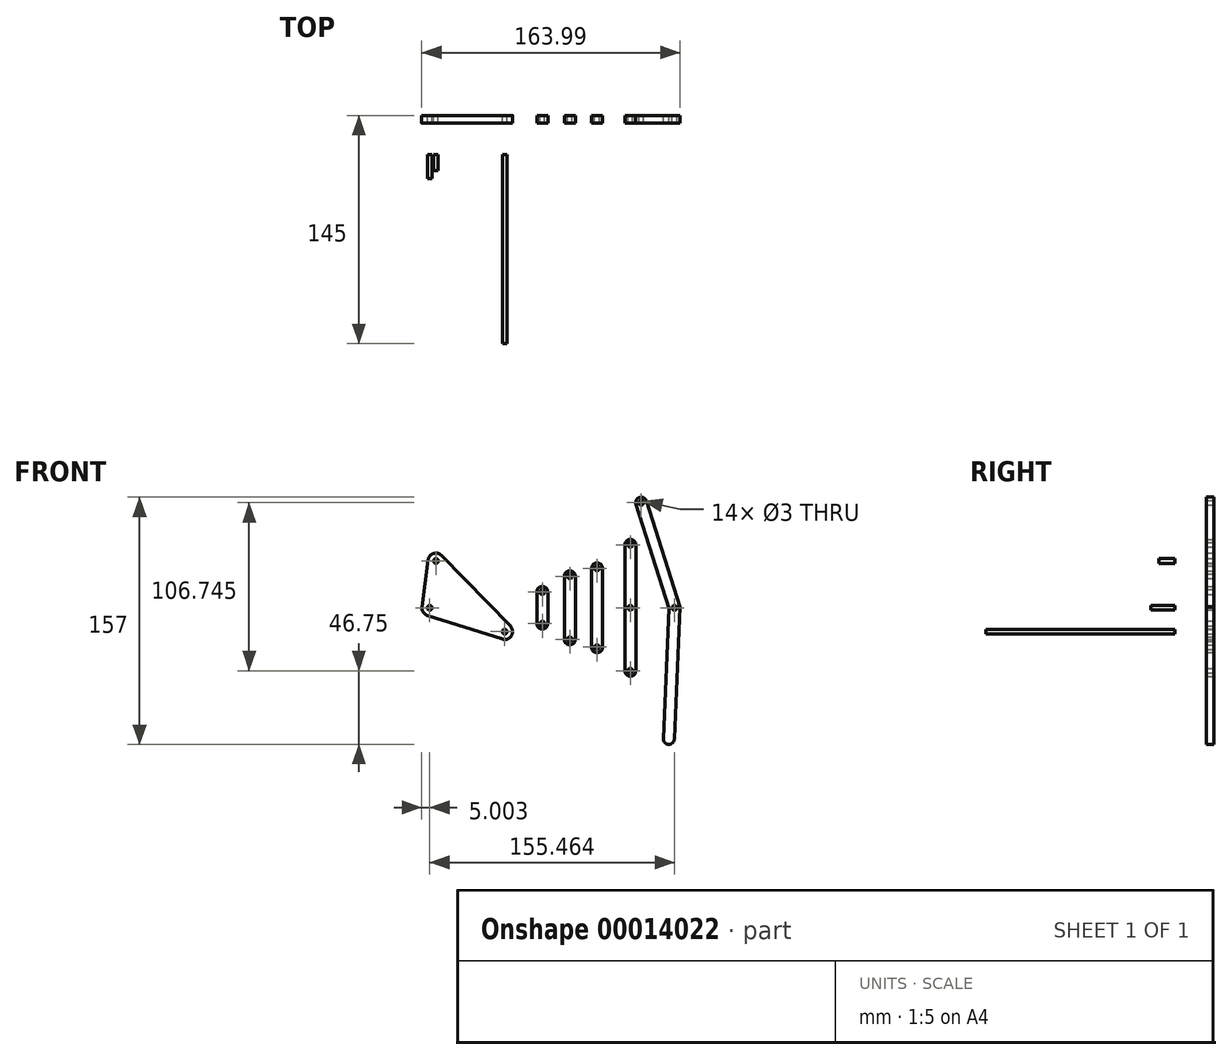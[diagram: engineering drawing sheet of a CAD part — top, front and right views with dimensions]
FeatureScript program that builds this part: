
annotation { "Feature Type Name" : "Feature", "Feature Type Description" : "" }
export const myFeature = defineFeature(function(context is Context, id is Id, definition is map)
    precondition{}
    {
        {
            var Q0;
            Q0=qCreatedBy(makeId("Front.planeOp"),FACE);
            var sketch = newSketch(context, id + "F0", { "sketchPlane" : qUnion([Q0])});
            skLineSegment(sketch, "E0", {"start": v(-62.83, 10) * mm, "end": v(-62.83, -10) * mm, "construction": true});
            skLineSegment(sketch, "E1", {"start": v(-45.34, 20) * mm, "end": v(-45.34, -20) * mm, "construction": true});
            skLineSegment(sketch, "E2", {"start": v(-28.03, 25) * mm, "end": v(-28.03, -25) * mm, "construction": true});
            skLineSegment(sketch, "E3", {"start": v(-6.9, 40) * mm, "end": v(-6.9, -40) * mm, "construction": true});
            skLineSegment(sketch, "E4", {"start": v(0, 66.75) * mm, "end": v(21.1, 0) * mm, "construction": true});
            skLineSegment(sketch, "E5", {"start": v(21.1, 0) * mm, "end": v(17.52, -83.25) * mm, "construction": true});
            skPoint(sketch, "E6", {"position": v(-62.83, 0) * mm});
            skPoint(sketch, "E7", {"position": v(-45.34, 0) * mm});
            skPoint(sketch, "E8", {"position": v(-28.03, 0) * mm});
            skPoint(sketch, "E9", {"position": v(-6.9, 0) * mm});
            skLineSegment(sketch, "E10", {"start": v(-130.38, 29.73) * mm, "end": v(-134.37, 0) * mm, "construction": true});
            skLineSegment(sketch, "E11", {"start": v(-134.37, 0) * mm, "end": v(-86.72, -15.14) * mm, "construction": true});
            skLineSegment(sketch, "E12", {"start": v(-86.72, -15.14) * mm, "end": v(-130.38, 29.73) * mm, "construction": true});
            skCircle(sketch, "E13", {"center": v(-62.83, 10) * mm, "radius": 1.5 * mm});
            skCircle(sketch, "E14", {"center": v(-62.83, -10) * mm, "radius": 1.5 * mm});
            skCircle(sketch, "E15", {"center": v(-45.34, -20) * mm, "radius": 1.5 * mm});
            skCircle(sketch, "E16", {"center": v(-45.34, 20) * mm, "radius": 1.5 * mm});
            skCircle(sketch, "E17", {"center": v(-28.03, 25) * mm, "radius": 1.5 * mm});
            skCircle(sketch, "E18", {"center": v(-28.03, -25) * mm, "radius": 1.5 * mm});
            skCircle(sketch, "E19", {"center": v(-6.9, 40) * mm, "radius": 1.5 * mm});
            skCircle(sketch, "E20", {"center": v(-6.9, -40) * mm, "radius": 1.5 * mm});
            skCircle(sketch, "E21", {"center": v(-6.9, 0) * mm, "radius": 1.5 * mm});
            skCircle(sketch, "E22", {"center": v(21.1, 0) * mm, "radius": 1.5 * mm});
            skCircle(sketch, "E23", {"center": v(0, 66.75) * mm, "radius": 1.5 * mm});
            skCircle(sketch, "E24", {"center": v(-130.38, 29.73) * mm, "radius": 1.5 * mm});
            skCircle(sketch, "E25", {"center": v(-134.37, 0) * mm, "radius": 1.5 * mm});
            skCircle(sketch, "E26", {"center": v(-86.72, -15.14) * mm, "radius": 1.5 * mm});
            skLineSegment(sketch, "E27.bottom", {"start": v(-66.33, 10) * mm, "end": v(-59.33, 10) * mm, "construction": true});
            skLineSegment(sketch, "E27.top", {"start": v(-66.33, -10) * mm, "end": v(-59.33, -10) * mm, "construction": true});
            skLineSegment(sketch, "E27.left", {"start": v(-66.33, 10) * mm, "end": v(-66.33, -10) * mm});
            skLineSegment(sketch, "E27.right", {"start": v(-59.33, 10) * mm, "end": v(-59.33, -10) * mm});
            skLineSegment(sketch, "E28.bottom", {"start": v(-48.84, 20) * mm, "end": v(-41.84, 20) * mm, "construction": true});
            skLineSegment(sketch, "E28.top", {"start": v(-48.84, -20) * mm, "end": v(-41.84, -20) * mm, "construction": true});
            skLineSegment(sketch, "E28.left", {"start": v(-48.84, 20) * mm, "end": v(-48.84, -20) * mm});
            skLineSegment(sketch, "E28.right", {"start": v(-41.84, 20) * mm, "end": v(-41.84, -20) * mm});
            skLineSegment(sketch, "E29.bottom", {"start": v(-31.53, 25) * mm, "end": v(-24.53, 25) * mm, "construction": true});
            skLineSegment(sketch, "E29.top", {"start": v(-31.53, -25) * mm, "end": v(-24.53, -25) * mm, "construction": true});
            skLineSegment(sketch, "E29.left", {"start": v(-31.53, 25) * mm, "end": v(-31.53, -25) * mm});
            skLineSegment(sketch, "E29.right", {"start": v(-24.53, 25) * mm, "end": v(-24.53, -25) * mm});
            skLineSegment(sketch, "E30.bottom", {"start": v(-10.4, 40) * mm, "end": v(-3.4, 40) * mm, "construction": true});
            skLineSegment(sketch, "E30.top", {"start": v(-10.4, -40) * mm, "end": v(-3.4, -40) * mm, "construction": true});
            skLineSegment(sketch, "E30.left", {"start": v(-10.4, 40) * mm, "end": v(-10.4, -40) * mm});
            skLineSegment(sketch, "E30.right", {"start": v(-3.4, 40) * mm, "end": v(-3.4, -40) * mm});
            skArc(sketch, "E31", {"start": v(-3.4, 40) * mm, "mid": v(-6.9, 43.5) * mm, "end": v(-10.4, 40) * mm});
            skArc(sketch, "E32", {"start": v(-24.53, 25) * mm, "mid": v(-28.03, 28.5) * mm, "end": v(-31.53, 25) * mm});
            skArc(sketch, "E33", {"start": v(-41.84, 20) * mm, "mid": v(-45.34, 23.5) * mm, "end": v(-48.84, 20) * mm});
            skArc(sketch, "E34", {"start": v(-59.33, 10) * mm, "mid": v(-62.83, 13.5) * mm, "end": v(-66.33, 10) * mm});
            skArc(sketch, "E35", {"start": v(-66.33, -10) * mm, "mid": v(-62.83, -13.5) * mm, "end": v(-59.33, -10) * mm});
            skArc(sketch, "E36", {"start": v(-48.84, -20) * mm, "mid": v(-45.34, -23.5) * mm, "end": v(-41.84, -20) * mm});
            skArc(sketch, "E37", {"start": v(-31.53, -25) * mm, "mid": v(-28.03, -28.5) * mm, "end": v(-24.53, -25) * mm});
            skArc(sketch, "E38", {"start": v(-10.4, -40) * mm, "mid": v(-6.9, -43.5) * mm, "end": v(-3.4, -40) * mm});
            skLineSegment(sketch, "E39.bottom", {"start": v(-3.34, 65.7) * mm, "end": v(3.34, 67.8) * mm, "construction": true});
            skLineSegment(sketch, "E39.top", {"start": v(17.57, -0.47) * mm, "end": v(24.62, 0.47) * mm, "construction": true});
            skLineSegment(sketch, "E39.left", {"start": v(3.34, 67.8) * mm, "end": v(24.62, 0.47) * mm});
            skLineSegment(sketch, "E39.right", {"start": v(-3.34, 65.7) * mm, "end": v(17.57, -0.47) * mm});
            skArc(sketch, "E40", {"start": v(3.34, 67.8) * mm, "mid": v(-1.05, 70.08) * mm, "end": v(-3.34, 65.7) * mm});
            skLineSegment(sketch, "E41", {"start": v(14.02, -83.1) * mm, "end": v(21.02, -83.4) * mm, "construction": true});
            skLineSegment(sketch, "E42", {"start": v(14.02, -83.1) * mm, "end": v(17.57, -0.47) * mm});
            skLineSegment(sketch, "E43", {"start": v(24.62, 0.47) * mm, "end": v(21.02, -83.4) * mm});
            skArc(sketch, "E44", {"start": v(14.02, -83.1) * mm, "mid": v(17.37, -86.75) * mm, "end": v(21.02, -83.4) * mm});
            skCircle(sketch, "E45", {"center": v(-130.38, 29.73) * mm, "radius": 5 * mm, "construction": true});
            skCircle(sketch, "E46", {"center": v(-134.37, 0) * mm, "radius": 5 * mm, "construction": true});
            skCircle(sketch, "E47", {"center": v(-86.72, -15.14) * mm, "radius": 5 * mm, "construction": true});
            skLineSegment(sketch, "E48", {"start": v(-83.13, -11.66) * mm, "end": v(-126.8, 33.22) * mm});
            skLineSegment(sketch, "E49", {"start": v(-135.34, 30.4) * mm, "end": v(-139.32, 0.66) * mm});
            skLineSegment(sketch, "E50", {"start": v(-135.88, -4.77) * mm, "end": v(-88.23, -19.9) * mm});
            skArc(sketch, "E51", {"start": v(-126.8, 33.22) * mm, "mid": v(-131.95, 34.48) * mm, "end": v(-135.34, 30.4) * mm});
            skArc(sketch, "E52", {"start": v(-139.32, 0.66) * mm, "mid": v(-138.6, -2.68) * mm, "end": v(-135.88, -4.77) * mm});
            skArc(sketch, "E53", {"start": v(-88.23, -19.9) * mm, "mid": v(-82.46, -17.77) * mm, "end": v(-83.13, -11.66) * mm});
            skSolve(sketch);
        }
        {
            var Q0;
            Q0=makeQuery(id+"F0.imprint","IMPRINT",FACE,{"disambiguationData":[TD([[makeQuery(id+"F0.imprint","IMPRINT",EDGE,{"derivedFrom":sQuery(id+"F0.wireOp",EDGE,"E24")}),-1.0]])]});
            var Q1;
            Q1=makeQuery(id+"F0.imprint","IMPRINT",FACE,{"disambiguationData":[TD([[makeQuery(id+"F0.imprint","IMPRINT",EDGE,{"derivedFrom":sQuery(id+"F0.wireOp",EDGE,"E13")}),-1.0]])]});
            var Q2;
            Q2=makeQuery(id+"F0.imprint","IMPRINT",FACE,{"disambiguationData":[TD([[makeQuery(id+"F0.imprint","IMPRINT",EDGE,{"derivedFrom":sQuery(id+"F0.wireOp",EDGE,"E15")}),-1.0]])]});
            var Q3;
            Q3=makeQuery(id+"F0.imprint","IMPRINT",FACE,{"disambiguationData":[TD([[makeQuery(id+"F0.imprint","IMPRINT",EDGE,{"derivedFrom":sQuery(id+"F0.wireOp",EDGE,"E17")}),-1.0]])]});
            var Q4;
            Q4=makeQuery(id+"F0.imprint","IMPRINT",FACE,{"disambiguationData":[TD([[makeQuery(id+"F0.imprint","IMPRINT",EDGE,{"derivedFrom":sQuery(id+"F0.wireOp",EDGE,"E19")}),-1.0]])]});
            var Q5;
            Q5=makeQuery(id+"F0.imprint","IMPRINT",FACE,{"disambiguationData":[TD([[makeQuery(id+"F0.imprint","IMPRINT",EDGE,{"derivedFrom":sQuery(id+"F0.wireOp",EDGE,"E22")}),-1.0]])]});
            extrude(context, id + "F1", {"entities" : qUnion([Q0, Q1, Q2, Q3, Q4, Q5]), "depth" : 5 * mm});
        }
        {
            var Q0;
            Q0=makeQuery(id+"F0.imprint","IMPRINT",FACE,{"disambiguationData":[TD([[makeQuery(id+"F0.imprint","IMPRINT",EDGE,{"derivedFrom":sQuery(id+"F0.wireOp",EDGE,"E24")}),1.0]])]});
            extrude(context, id + "F2", {"entities" : qUnion([Q0]), "operationType" : NewBodyOperationType.ADD, "depth" : 35 * mm, "hasSecondDirection" : true, "secondDirectionOppositeDirection" : false, "secondDirectionDepth" : 25 * mm});
        }
        {
            var Q0;
            Q0=makeQuery(id+"F0.imprint","IMPRINT",FACE,{"disambiguationData":[TD([[makeQuery(id+"F0.imprint","IMPRINT",EDGE,{"derivedFrom":sQuery(id+"F0.wireOp",EDGE,"E25")}),1.0]])]});
            extrude(context, id + "F3", {"entities" : qUnion([Q0]), "depth" : 40 * mm, "hasSecondDirection" : true, "secondDirectionOppositeDirection" : false, "secondDirectionDepth" : 25 * mm});
        }
        {
            var Q0;
            Q0=makeQuery(id+"F0.imprint","IMPRINT",FACE,{"disambiguationData":[TD([[makeQuery(id+"F0.imprint","IMPRINT",EDGE,{"derivedFrom":sQuery(id+"F0.wireOp",EDGE,"E26")}),1.0]])]});
            extrude(context, id + "F4", {"entities" : qUnion([Q0]), "depth" : 145 * mm, "hasSecondDirection" : true, "secondDirectionOppositeDirection" : false, "secondDirectionDepth" : 25 * mm});
        }
    });
